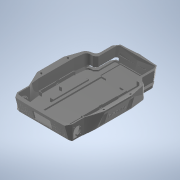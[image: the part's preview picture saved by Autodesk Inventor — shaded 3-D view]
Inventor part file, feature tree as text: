
AUTODESK INVENTOR PART (.ipt)
format: ipt  version: 2020 (Build 240168000, 168)  size: 7,441,408 bytes
history: native  units: mm
features: other x95, surface_op x82, extrude x24, sketch x21, mirror x8, projected_geometry x6, plane x5, fillet x4, chamfer x3, split x2, delete_face x1, shell x1, boolean_combine x1, move_body x1, hole x1, pattern_linear x1, loft x1
ambient origin geometry x8: Origin, YZ Plane, XZ Plane, XY Plane, X Axis, Y Axis, Z Axis, Center Point
bodies: Solid1 (feature_tree), Solid2 (feature_tree)
feature tree (257):
  other  "deck.ipt"
  delete_face  "Delete Face1"
  extrude  "Extrusion1"  Depth=1.5mm
  extrude  "Extrusion2"  Depth=3.0mm TaperAngle=0.0deg
  extrude  "Extrusion19"  Depth=1.5mm
  extrude  "Extrusion3"  Depth=62.0mm
  sketch  "Sketch3"  dims[d0=80.5mm d2=1.5mm]
  extrude  "Extrusion4"  Depth=39.6mm
  extrude  "Extrusion5"  Depth=2.0mm
  mirror  "Mirror1"
  plane  "Work Plane2"
  sketch  "Sketch4"  dims[d3=3.0mm d4=3.0mm d5=0.0mm]
  plane  "Work Plane3"
  extrude  "Extrusion6"  Depth=2.0mm
  extrude  "Extrusion7"  Depth=2.0mm
  fillet  "Fillet1"  Radius=2.0mm
  fillet  "Fillet2"  Radius=59.7mm
  plane  "Work Plane4"
  sketch  "Sketch7"  dims[d9=19.0mm d10=62.0mm]
  sketch  "Sketch8"  dims[d11=1.0mm d12=0.0mm d14=39.6mm]
  sketch  "Sketch9"  dims[d15=3.0mm d16=2.0mm]
  extrude  "Extrusion8"  Depth=3.0mm TaperAngle=0.0deg
  surface_op  "Sculpt1"
  shell  "Shell1"  Thickness=13.0mm
  boolean_combine  "Combine1"
  extrude  "Extrusion9"  Depth=32.2mm
  extrude  "Extrusion11"  Depth=5.0mm
  extrude  "Extrusion10"  Depth=19.0mm
  mirror  "Mirror2"
  chamfer  "Chamfer1"  Distance=6.0mm
  chamfer  "Chamfer2"  Distance=3.0mm
  move_body  "Move Body1"
  extrude  "Extrusion12"  Depth=6.0mm TaperAngle=0.0deg
  fillet  "Fillet3"  Radius=2.0mm
  extrude  "Extrusion13"  Depth=0.5mm
  extrude  "Extrusion14"  Depth=42.0mm
  mirror  "Mirror3"
  mirror  "Mirror4"
  hole  "Hole1"  [1 undecoded]
  plane  "Work Plane5"
  extrude  "Extrusion15"  Depth=15.0mm
  pattern_linear  "Rectangular Pattern1"  Spacing1=13.0mm  [1 undecoded]
  mirror  "Mirror5"
  extrude  "Extrusion16"  Depth=4.0mm
  extrude  "Extrusion17"  Depth=2.0mm TaperAngle=0.0deg
  split  "Split1"
  fillet  "Fillet5"  [1 undecoded]
  extrude  "Extrusion20"  TaperAngle=0.0deg  [1 undecoded]
  mirror  "Mirror7"
  extrude  "Extrusion21"  Depth=5.0mm
  extrude  "Extrusion22"  TaperAngle=0.0deg  [1 undecoded]
  chamfer  "Chamfer3"  Distance=5.0mm
  split  "Split2"
  extrude  "Extrusion23"  TaperAngle=0.0deg  [1 undecoded]
  mirror  "Mirror8"
  extrude  "Extrusion24"  Depth=3.0mm
  plane  "Work Plane6"
  sketch  "Sketch29"  dims[d47=1.0mm d49=6.0mm d50=0.0mm d51=3.0mm d52=6.0mm d53=0.0mm d54=2.0mm d55=0.5mm d56=42.0mm d57=2.0mm d58=15.0mm d59=13.0mm d60=4.0mm d61=2.0mm d62=0.0mm d63=0.0mm d64=90.0deg d65=0.0mm d66=90.0deg d100=5.0mm d101=0.0mm d102=5.0mm d103=0.0mm d104=3.0mm d105=10.0mm d106=0.0mm d107=10.0mm d108=0.0mm d109=10.0mm d110=0.0mm d111=2.5mm d112=2.0mm d113=45.0deg d114=2.5mm d115=2.0mm d116=45.0deg d117=10.0mm d118=385.0mm d119=0.0mm d120=0.0mm d121=54.0mm d122=0.0mm d123=7.5mm d124=15.0mm d125=80.0mm d127=5.5mm d128=6.0mm d129=4.0mm d130=2.0mm d131=90.0deg d132=8.0mm d133=20.594885mm d135=10.0mm d136=0.0mm d137=12.0mm d140=16.442mm d141=0.0mm d142=8.0mm d143=32.0mm d144=2.0mm d146=39.6mm d148=0.0mm d150=143.0mm d151=0.0mm d154=5.5mm d155=15.0mm d156=0.0mm d157=20.0mm d159=80.0mm d160=53.5mm d161=25.5mm d162=148.0mm d163=74.0mm d164=7.0mm d165=10.0mm d166=0.0mm d167=53.5mm d168=26.75mm d170=10.0mm d171=25.5mm d172=12.75mm d173=10.0mm d174=0.0mm d175=59.0mm d176=2.5mm d177=2.0mm d180=2.0mm d181=68.0mm d183=1.5mm d184=3.0mm d187=7.0mm d188=0.0mm d190=32.0mm d191=17.0mm d192=5.0mm d193=7.0mm d194=10.0mm d195=0.0mm d196=95.0mm d197=7.0mm d198=1.5mm d199=0.0mm d200=183.5mm d201=7.0mm d203=4.2mm d204=10.0mm d205=44.0mm d206=1.5mm d207=10.0mm d208=8.0mm d209=0.0mm d210=8.0mm d211=2.0mm d212=45.0deg d213=1.0mm d214=0.0mm d215=1.0mm d216=1.5mm d217=2.0mm d218=2.5mm d220=3.0mm d222=1.5mm d223=1.5mm d224=1.5mm d226=1.0mm d227=0.0mm d228=1.5mm d230=2.0mm d231=1.5mm d232=1.5mm d233=1.5mm d234=0.5mm d235=0.6mm d236=1.5mm d237=0.8mm d238=1.5mm d239=0.9mm d242=1.5mm d243=1.5mm d244=0.8mm d245=1.5mm d246=0.6mm d247=1.5mm d248=3.5mm d249=4.0mm d250=1.5mm d251=1.5mm d252=1.5mm d253=1.5mm d254=3.5mm d255=4.0mm d256=1.5mm d257=1.5mm d258=1.5mm d259=1.5mm d260=210.0mm d262=6.775mm d263=10.0mm d265=10.0mm d267=1.5mm d268=1.5mm d269=3.0435mm d270=3.043244mm d271=0.5mm d272=0.0mm d273=1.0mm d274=1.5mm d275=2.0mm d276=2.5mm d277=3.0mm d278=1.5mm d279=1.5mm d280=1.5mm d281=1.0mm d282=0.0mm d283=1.5mm d284=2.0mm d285=1.5mm d286=1.5mm d287=1.5mm d288=0.5mm d289=0.6mm d290=1.5mm d291=0.8mm d292=1.5mm d293=0.9mm d294=1.5mm d295=1.5mm d296=0.8mm d297=1.5mm d298=0.6mm d299=1.5mm d300=3.5mm d301=4.0mm d302=1.5mm d303=1.5mm d304=3.5mm d305=4.0mm d306=1.5mm d307=1.5mm d308=1.5mm d309=1.5mm d310=1.5mm d311=1.5mm d312=1.5mm d313=170.0mm d315=6.7mm d316=10.0mm d318=10.0mm d320=1.5mm d321=1.62mm d322=1.619738mm d323=0.5mm d324=0.5mm d325=0.0mm d326=0.0mm d327=0.0mm d328=0.0mm d329=0.0mm d330=0.0mm d331=0.0mm d332=0.0mm d333=0.0mm d334=0.0mm d335=0.0mm d336=0.0mm d337=0.0mm d338=0.0mm d339=0.0mm d340=0.0mm d341=0.0mm d342=0.0mm d343=0.0mm d344=0.0mm d345=0.0mm d346=0.0mm d347=0.0mm d348=0.0mm d349=0.0mm d350=0.0mm d351=0.0mm d352=0.0mm d353=0.0mm d354=0.0mm d355=0.0mm d356=0.0mm d357=0.0mm d358=0.0mm d359=0.0mm d360=0.0mm d361=0.0mm d362=0.0mm d363=0.0mm d364=0.0mm d365=0.0mm d366=0.0mm d367=0.0mm d368=0.0mm d369=0.0mm d370=0.0mm d371=0.0mm d372=0.0mm d373=0.0mm d374=0.0mm d375=0.0mm d376=0.0mm d377=0.0mm d378=0.0mm d379=0.0mm d380=0.0mm d381=0.0mm d382=0.0mm d383=0.0mm d384=0.0mm d385=0.0mm d386=0.0mm d387=0.0mm d388=0.0mm d389=0.0mm d390=0.0mm d391=0.0mm d392=0.0mm d393=0.0mm d394=0.0mm d395=0.0mm d396=0.0mm d397=0.0mm d398=0.0mm d399=0.0mm d400=0.0mm d401=0.0mm d134=1.0mm d138=5.5mm d139=0.375mm d145=0.375mm]
  sketch  "3D Sketch2"
  sketch  "3D Sketch3"
  surface_op  "Sculpt2"
  mirror  "Mirror9"
  sketch  "Sketch6"  dims[d6=9.0mm d7=0.0mm d8=1.5mm]
  other  "Edges1"
  other  "Srf1"
  other  "Srf16"
  other  "Srf17"
  sketch  "Sketch10"  dims[d17=103.0mm d18=2.0mm]
  projected_geometry  "Projected Loop1"
  sketch  "Sketch11"  dims[d19=7.0mm d21=2.0mm d22=2.0mm d23=59.7mm]
  projected_geometry  "Projected Loop2"
  sketch  "Sketch12"  dims[d24=7.0mm d26=3.0mm d27=0.0mm d28=13.0mm d29=0.0mm]
  other  "Front Profile"
  other  "Srf18"
  sketch  "Sketch18"  dims[d30=25.7mm d31=32.2mm]
  projected_geometry  "Projected Loop3"
  sketch  "Sketch20"  dims[d32=23.0mm d33=5.0mm]
  other  "Work Axis1"
  other  "Work Axis2"
  sketch  "Sketch21"  dims[d34=-3.5mm d35=19.0mm]
  sketch  "Sketch22"  dims[d36=25.0mm]
  sketch  "Sketch24"  dims[d38=3.5mm]
  projected_geometry  "Projected Loop5"
  sketch  "Sketch25"  dims[d39=2.0mm]
  projected_geometry  "Projected Loop6"
  projected_geometry  "Projected Loop7"
  sketch  "Sketch26"  dims[d43=-3.5mm]
  sketch  "Sketch27"  dims[d44=12.6mm]
  sketch  "Sketch28"  dims[d45=7.0mm]
  other  "Project to Surface1"
  other  "Srf20"
  other  "Project to Surface2"
  other  "Srf21"
  other  "Srf22"
  other  "Srf23"
  other  "Srf24"
  other  "Srf25"
  other  "Srf26"
  other  "Srf27"
  other  "Srf28"
  other  "Srf29"
  other  "Srf30"
  other  "Srf31"
  other  "Srf32"
  other  "Srf33"
  other  "Srf34"
  other  "Srf35"
  other  "Srf36"
  other  "Srf37"
  other  "Srf38"
  other  "Srf39"
  other  "Srf40"
  other  "Srf41"
  other  "Srf42"
  other  "Srf43"
  other  "Srf44"
  other  "Srf45"
  other  "Srf46"
  other  "Srf47"
  other  "Srf48"
  other  "Srf49"
  other  "Srf50"
  other  "Srf51"
  other  "Srf52"
  other  "Srf53"
  other  "Srf54"
  other  "Srf55"
  other  "Srf56"
  other  "Srf57"
  other  "Srf58"
  other  "Srf59"
  other  "Srf60"
  other  "Srf61"
  other  "Srf62"
  other  "Srf63"
  other  "Srf64"
  other  "Srf65"
  other  "Srf66"
  other  "Srf67"
  other  "Srf68"
  other  "Srf69"
  other  "Srf70"
  other  "Srf71"
  other  "Srf72"
  other  "Srf73"
  other  "Srf74"
  other  "Srf75"
  other  "Srf76"
  other  "Srf77"
  other  "Srf78"
  other  "Srf79"
  other  "Srf80"
  other  "Srf81"
  other  "Srf82"
  other  "Srf83"
  other  "Srf84"
  other  "Srf85"
  other  "Srf86"
  other  "Srf87"
  other  "Srf88"
  other  "Srf89"
  other  "Srf90"
  other  "Srf91"
  other  "Srf92"
  other  "Srf93"
  other  "Srf94"
  other  "Srf95"
  other  "Srf96"
  other  "Srf97"
  extrude  "ExtrusionSrf1"  Depth=10.0mm TaperAngle=0.0deg
  surface_op  "Surface1"
  other  "OffsetSrf2"
  loft  "LoftSrf1"
  surface_op  "Boundary Patch13"
  surface_op  "Boundary Patch14"
  other  "Srf19"
  surface_op  "Boundary Patch15"
  surface_op  "Boundary Patch16"
  surface_op  "Boundary Patch17"
  surface_op  "Boundary Patch18"
  surface_op  "Boundary Patch19"
  surface_op  "Boundary Patch20"
  surface_op  "Boundary Patch22"
  surface_op  "Boundary Patch23"
  surface_op  "Boundary Patch24"
  surface_op  "Boundary Patch25"
  surface_op  "Boundary Patch26"
  surface_op  "Boundary Patch27"
  surface_op  "Boundary Patch28"
  surface_op  "Boundary Patch29"
  surface_op  "Boundary Patch30"
  surface_op  "Boundary Patch31"
  surface_op  "Boundary Patch32"
  surface_op  "Boundary Patch33"
  surface_op  "Boundary Patch34"
  surface_op  "Boundary Patch35"
  surface_op  "Boundary Patch36"
  surface_op  "Boundary Patch37"
  surface_op  "Boundary Patch38"
  surface_op  "Boundary Patch39"
  surface_op  "Boundary Patch40"
  surface_op  "Boundary Patch41"
  surface_op  "Boundary Patch42"
  surface_op  "Boundary Patch43"
  surface_op  "Boundary Patch44"
  surface_op  "Boundary Patch45"
  surface_op  "Boundary Patch46"
  surface_op  "Boundary Patch47"
  surface_op  "Boundary Patch48"
  surface_op  "Boundary Patch49"
  surface_op  "Boundary Patch50"
  surface_op  "Boundary Patch51"
  surface_op  "Boundary Patch52"
  surface_op  "Boundary Patch53"
  surface_op  "Boundary Patch54"
  surface_op  "Boundary Patch55"
  surface_op  "Boundary Patch56"
  surface_op  "Boundary Patch57"
  surface_op  "Boundary Patch58"
  surface_op  "Boundary Patch59"
  surface_op  "Boundary Patch60"
  surface_op  "Boundary Patch61"
  surface_op  "Boundary Patch62"
  surface_op  "Boundary Patch63"
  surface_op  "Boundary Patch64"
  surface_op  "Boundary Patch65"
  surface_op  "Boundary Patch66"
  surface_op  "Boundary Patch67"
  surface_op  "Boundary Patch68"
  surface_op  "Boundary Patch69"
  surface_op  "Boundary Patch70"
  surface_op  "Boundary Patch71"
  surface_op  "Boundary Patch72"
  surface_op  "Boundary Patch73"
  surface_op  "Boundary Patch74"
  surface_op  "Boundary Patch75"
  surface_op  "Boundary Patch76"
  surface_op  "Boundary Patch77"
  surface_op  "Boundary Patch78"
  surface_op  "Boundary Patch79"
  surface_op  "Boundary Patch80"
  surface_op  "Boundary Patch81"
  surface_op  "Boundary Patch82"
  surface_op  "Boundary Patch83"
  surface_op  "Boundary Patch84"
  surface_op  "Boundary Patch85"
  surface_op  "Boundary Patch86"
  surface_op  "Boundary Patch87"
  surface_op  "Boundary Patch88"
  surface_op  "Boundary Patch89"
  surface_op  "Boundary Patch90"
  surface_op  "Boundary Patch91"
  surface_op  "Boundary Patch21"
  parser-record x1  (decoder bookkeeping rows leaked as tree rows — omitted from the tree; the rows remain in map.json)
  other  "Housing v3.iam"
  other  "Receiver:1"
  other  "Receiver Case:1"
note: 6 required parameter values undecoded (feature->parameter linkage not recoverable at this tier; creation-order binding heuristic only, values carry confidence <= 0.55)
note: 1 file-system path scrubbed to <path> (originals preserved in map.json)
